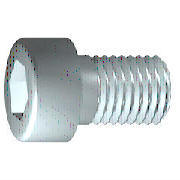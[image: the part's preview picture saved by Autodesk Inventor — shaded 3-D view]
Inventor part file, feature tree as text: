
AUTODESK INVENTOR PART (.ipt)
format: ipt  version: 2023.2 (Build 272271030, 271C)  size: 188,416 bytes
history: native  units: mm (DEFAULTED — no unit token found)
features: sketch x2, other x1, extrude x1, plane x1, fillet x1
ambient origin geometry x7: Origin, YZ Plane, XY Plane, X Axis, Y Axis, Z Axis, Center Point
bodies: Solid1 (feature_tree)
feature tree (6):
  other  "Körper"
  extrude  "Loch"  Depth=3.0mm
  plane  "Work Plane1"
  fillet  "Fillet2"  Radius=3.0mm
  sketch  "Skizze1"  dims[d1=18.75mm d2=0.306825mm d3=3.0mm]
  sketch  "Skizze2"  dims[d4=1.3mm d5=60.0deg d6=3.0mm d7=3.0mm d8=2.886751mm d9=5.5mm d10=90.0deg d11=10.0mm d12=0.0mm d13=18.75mm d14=0.0mm d15=0.306725mm d16=0.306725mm d17=0.3mm d19=0.0mm d26=20.0mm d27=45.0deg d28=0.0mm d29=0.0mm d30=0.1mm]
